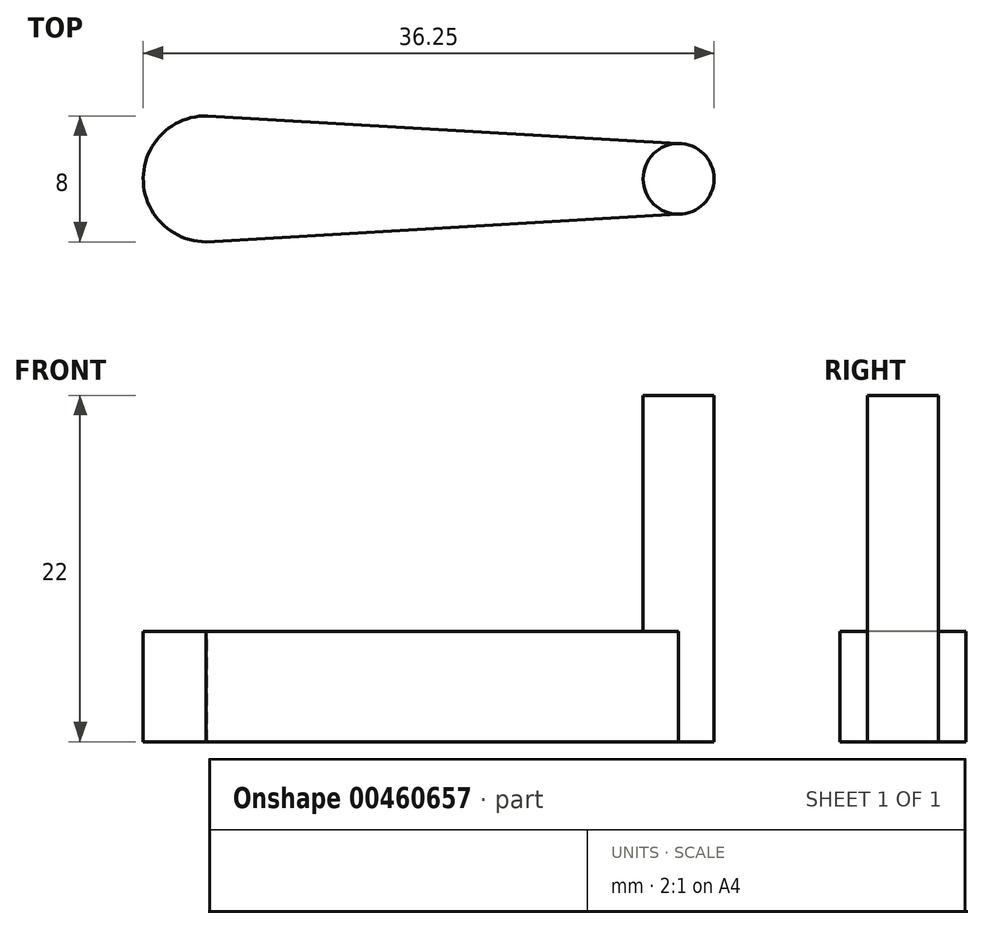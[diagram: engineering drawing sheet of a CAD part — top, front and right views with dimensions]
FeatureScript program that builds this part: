
annotation { "Feature Type Name" : "Feature", "Feature Type Description" : "" }
export const myFeature = defineFeature(function(context is Context, id is Id, definition is map)
    precondition{}
    {
        {
            var Q0;
            Q0=qCreatedBy(makeId("Top.planeOp"),FACE);
            var sketch = newSketch(context, id + "F0", { "sketchPlane" : qUnion([Q0])});
            skLineSegment(sketch, "E0", {"start": v(0, 0) * mm, "end": v(-30, 0) * mm});
            skCircle(sketch, "E1", {"center": v(0, 0) * mm, "radius": 2.25 * mm});
            skCircle(sketch, "E2", {"center": v(-30, 0) * mm, "radius": 4 * mm});
            skLineSegment(sketch, "E3", {"start": v(0, -2.25) * mm, "end": v(-30.01, -4) * mm});
            skLineSegment(sketch, "E4", {"start": v(0, 2.25) * mm, "end": v(-29.93, 4) * mm});
            skSolve(sketch);
        }
        {
            var Q0;
            {var subQ0=sQuery(id+"F0.wireOp",EDGE,"E1");var subQ1=makeQuery(id+"F0.imprint","INTERSECT",VERTEX,{"derivedFrom":[subQ0,sQuery(id+"F0.wireOp",EDGE,"E4")]});Q0=makeQuery(id+"F0.imprint","IMPRINT",FACE,{"disambiguationData":[TD([[makeQuery(id+"F0.imprint","IMPRINT",EDGE,{"disambiguationData":[TD([[subQ1,-1.0]])],"derivedFrom":subQ0}),1.0]])]});}
            extrude(context, id + "F1", {"entities" : qUnion([Q0]), "depth" : 15 * mm});
        }
        {
            var Q0;
            {var subQ0=sQuery(id+"F0.wireOp",EDGE,"E1");var subQ1=sQuery(id+"F0.wireOp",EDGE,"E0");var subQ2=makeQuery(id+"F0.imprint","INTERSECT",VERTEX,{"derivedFrom":[subQ1,subQ0]});Q0=makeQuery(id+"F0.imprint","IMPRINT",FACE,{"disambiguationData":[TD([[makeQuery(id+"F0.imprint","IMPRINT",EDGE,{"disambiguationData":[TD([[subQ2,-1.0]])],"derivedFrom":subQ1}),1.0]])]});}
            var Q1;
            {var subQ0=sQuery(id+"F0.wireOp",EDGE,"E1");var subQ1=sQuery(id+"F0.wireOp",EDGE,"E0");var subQ2=makeQuery(id+"F0.imprint","INTERSECT",VERTEX,{"derivedFrom":[subQ1,subQ0]});Q1=makeQuery(id+"F0.imprint","IMPRINT",FACE,{"disambiguationData":[TD([[makeQuery(id+"F0.imprint","IMPRINT",EDGE,{"disambiguationData":[TD([[subQ2,-1.0]])],"derivedFrom":subQ1}),-1.0]])]});}
            var Q2;
            {var subQ1=sQuery(id+"F0.wireOp",EDGE,"E2");var subQ4=makeQuery(id+"F0.imprint","INTERSECT",VERTEX,{"derivedFrom":[sQuery(id+"F0.wireOp",EDGE,"E0"),subQ1]});Q2=makeQuery(id+"F0.imprint","IMPRINT",FACE,{"disambiguationData":[TD([[makeQuery(id+"F0.imprint","IMPRINT",EDGE,{"disambiguationData":[TD([[subQ4,-1.0]])],"derivedFrom":subQ1}),1.0]])]});}
            var Q3;
            {var subQ0=sQuery(id+"F0.wireOp",EDGE,"E1");var subQ1=makeQuery(id+"F0.imprint","INTERSECT",VERTEX,{"derivedFrom":[subQ0,sQuery(id+"F0.wireOp",EDGE,"E4")]});Q3=makeQuery(id+"F0.imprint","IMPRINT",FACE,{"disambiguationData":[TD([[makeQuery(id+"F0.imprint","IMPRINT",EDGE,{"disambiguationData":[TD([[subQ1,-1.0]])],"derivedFrom":subQ0}),1.0]])]});}
            extrude(context, id + "F2", {"entities" : qUnion([Q0, Q1, Q2, Q3]), "operationType" : NewBodyOperationType.ADD, "oppositeDirection" : true, "depth" : 7 * mm});
        }
    });
